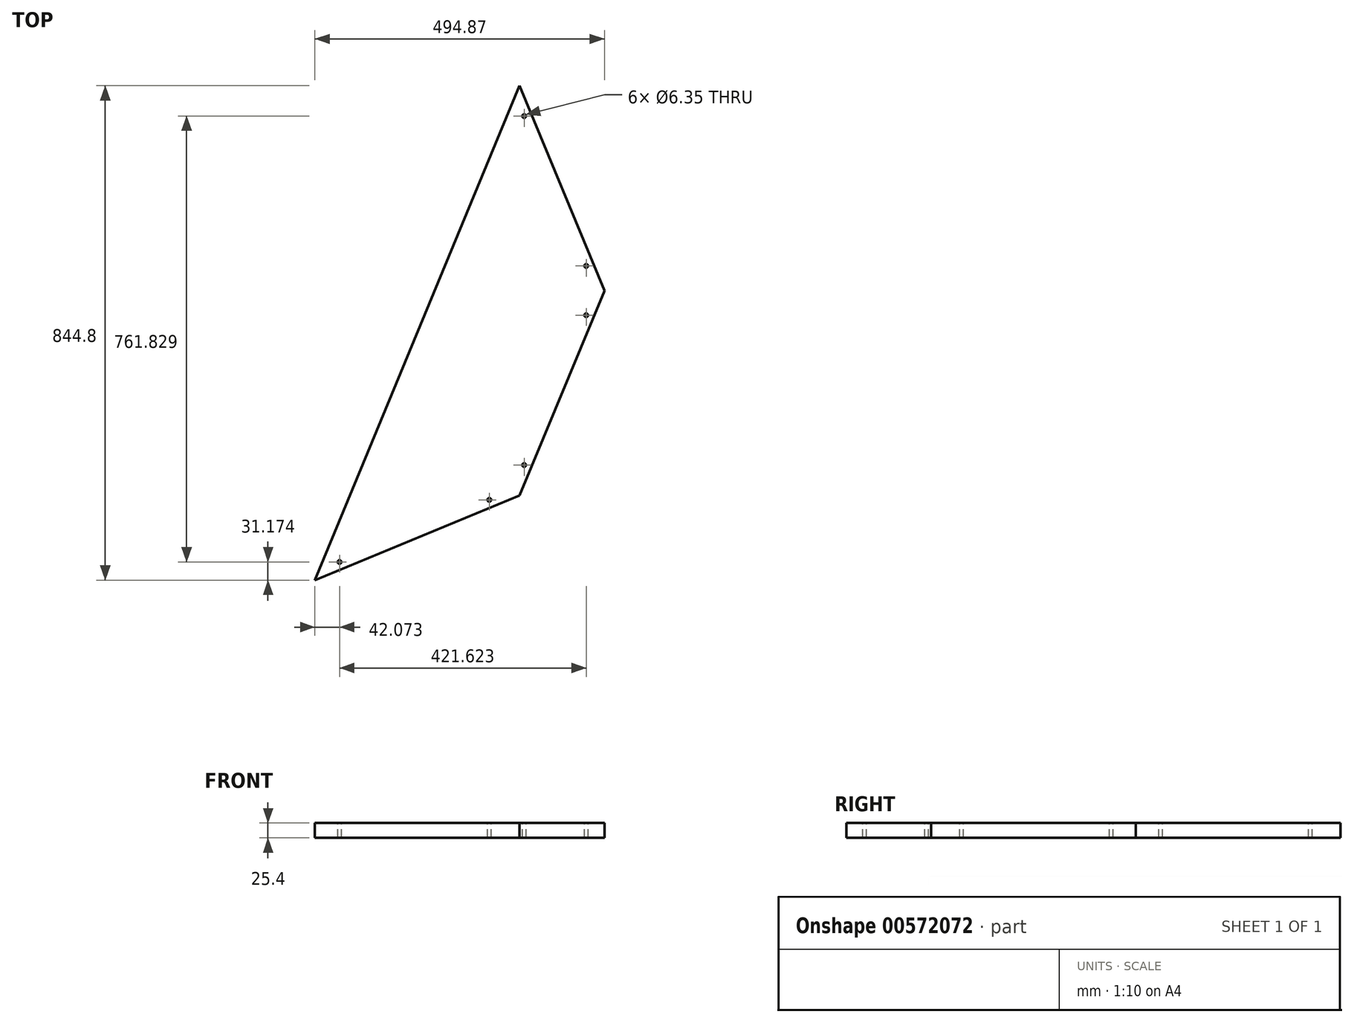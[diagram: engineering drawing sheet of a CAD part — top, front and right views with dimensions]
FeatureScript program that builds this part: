
annotation { "Feature Type Name" : "Feature", "Feature Type Description" : "" }
export const myFeature = defineFeature(function(context is Context, id is Id, definition is map)
    precondition{}
    {
        {
            var Q0;
            Q0=qCreatedBy(makeId("Top.planeOp"),FACE);
            var sketch = newSketch(context, id + "F0", { "sketchPlane" : qUnion([Q0])});
            skCircle(sketch, "E0.cCircle", {"center": v(0, 0) * mm, "radius": 494.87 * mm, "construction": true});
            skLineSegment(sketch, "E0.0", {"start": v(494.87, 0) * mm, "end": v(349.93, -349.93) * mm});
            skLineSegment(sketch, "E0.1", {"start": v(349.93, -349.93) * mm, "end": v(0, -494.87) * mm});
            skLineSegment(sketch, "E0.2", {"start": v(0, -494.87) * mm, "end": v(-349.93, -349.93) * mm});
            skLineSegment(sketch, "E0.3", {"start": v(-349.93, -349.93) * mm, "end": v(-494.87, 0) * mm});
            skLineSegment(sketch, "E0.4", {"start": v(-494.87, 0) * mm, "end": v(-349.93, 349.93) * mm});
            skLineSegment(sketch, "E0.5", {"start": v(-349.93, 349.93) * mm, "end": v(0, 494.87) * mm});
            skLineSegment(sketch, "E0.6", {"start": v(0, 494.87) * mm, "end": v(349.93, 349.93) * mm});
            skLineSegment(sketch, "E0.7", {"start": v(349.93, 349.93) * mm, "end": v(494.87, 0) * mm});
            skLineSegment(sketch, "E1", {"start": v(349.93, 349.93) * mm, "end": v(0, -494.87) * mm});
            skSolve(sketch);
        }
        {
            var Q0;
            Q0=makeQuery(id+"F0.imprint","IMPRINT",FACE,{"disambiguationData":[TD([[makeQuery(id+"F0.imprint","IMPRINT",EDGE,{"derivedFrom":sQuery(id+"F0.wireOp",EDGE,"E0.0")}),-1.0]])]});
            extrude(context, id + "F1", {"entities" : qUnion([Q0]), "depth" : 25.4 * mm, "offsetDistance" : 25.4 * mm});
        }
        {
            var Q0;
            Q0=makeQuery(id+"F1.opExtrude","CAP_FACE",FACE,{"disambiguationData":[OSD([sQuery(id+"F0.wireOp",EDGE,"E0.0"),sQuery(id+"F0.wireOp",EDGE,"E0.1"),sQuery(id+"F0.wireOp",EDGE,"E0.7"),sQuery(id+"F0.wireOp",EDGE,"E1")])],"isStart":false});
            var sketch = newSketch(context, id + "F2", { "sketchPlane" : qUnion([Q0])});
            skCircle(sketch, "E2", {"center": v(42.07, -463.7) * mm, "radius": 3.18 * mm});
            skCircle(sketch, "E3", {"center": v(298.13, -357.63) * mm, "radius": 3.17 * mm});
            skCircle(sketch, "E4", {"center": v(357.63, -298.13) * mm, "radius": 3.17 * mm});
            skCircle(sketch, "E5", {"center": v(463.7, -42.07) * mm, "radius": 3.17 * mm});
            skCircle(sketch, "E6", {"center": v(463.7, 42.07) * mm, "radius": 3.17 * mm});
            skCircle(sketch, "E7", {"center": v(357.63, 298.13) * mm, "radius": 3.18 * mm});
            skLineSegment(sketch, "E8", {"start": v(357.63, 298.13) * mm, "end": v(360.57, 299.35) * mm});
            skLineSegment(sketch, "E9", {"start": v(360.57, 299.35) * mm, "end": v(369.37, 303) * mm});
            skLineSegment(sketch, "E10", {"start": v(463.7, 42.07) * mm, "end": v(466.63, 43.29) * mm});
            skLineSegment(sketch, "E11", {"start": v(466.63, 43.29) * mm, "end": v(475.43, 46.93) * mm});
            skLineSegment(sketch, "E12", {"start": v(463.7, -42.07) * mm, "end": v(460.76, -40.86) * mm});
            skLineSegment(sketch, "E13", {"start": v(298.13, -357.63) * mm, "end": v(299.35, -360.57) * mm});
            skLineSegment(sketch, "E14", {"start": v(299.35, -360.57) * mm, "end": v(303, -369.37) * mm});
            skLineSegment(sketch, "E15", {"start": v(42.07, -463.7) * mm, "end": v(43.29, -466.63) * mm});
            skLineSegment(sketch, "E16", {"start": v(43.29, -466.63) * mm, "end": v(46.93, -475.43) * mm});
            skLineSegment(sketch, "E17", {"start": v(357.63, -298.13) * mm, "end": v(354.7, -296.92) * mm});
            skLineSegment(sketch, "E18", {"start": v(354.7, -296.92) * mm, "end": v(369.37, -303) * mm});
            skLineSegment(sketch, "E19", {"start": v(463.7, -42.07) * mm, "end": v(475.43, -46.93) * mm});
            skSolve(sketch);
        }
        {
            var Q0;
            Q0 = qSketchRegion(id + "F2", true);
            extrude(context, id + "F3", {"entities" : qUnion([Q0]), "operationType" : NewBodyOperationType.REMOVE, "endBound" : BoundingType.THROUGH_ALL, "oppositeDirection" : true, "depth" : 25.4 * mm, "offsetDistance" : 25.4 * mm});
        }
    });
